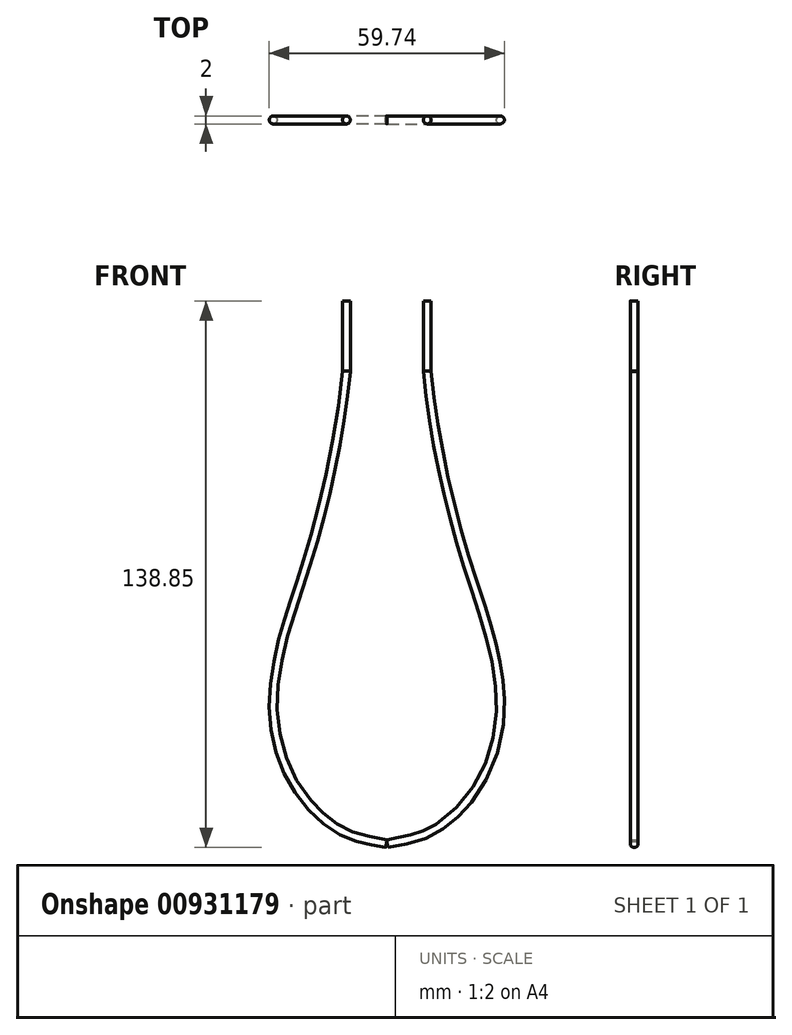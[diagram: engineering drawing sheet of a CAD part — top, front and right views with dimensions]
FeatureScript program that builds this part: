
annotation { "Feature Type Name" : "Feature", "Feature Type Description" : "" }
export const myFeature = defineFeature(function(context is Context, id is Id, definition is map)
    precondition{}
    {
        {
            var Q0;
            Q0=qCreatedBy(makeId("Front.planeOp"),FACE);
            var sketch = newSketch(context, id + "F0", { "sketchPlane" : qUnion([Q0])});
            skLineSegment(sketch, "E0", {"start": v(9.76, 64.47) * mm, "end": v(9.76, 46.63) * mm});
            skFitSpline(sketch, "E1", {"points": [v(9.76, 46.63) * mm, v(19.16, 0) * mm, v(25.18, -18.92) * mm, v(28.32, -40.13) * mm, v(22.05, -59.65) * mm, v(9.76, -70.5) * mm, v(0, -72.9) * mm], "startDerivative": vector(18.65, -207.85) * mm, "endDerivative": vector(-79.5, -16.58) * mm});
            skSolve(sketch);
        }
        {
            var Q0;
            Q0=qCreatedBy(makeId("Top.planeOp"),FACE);
            cPlane(context, id + "F1", {"entities" : qUnion([Q0]), "cplaneType" : CPlaneType.OFFSET, "offset" : 61.98 * mm, "width" : 152.4 * mm, "height" : 152.4 * mm});
        }
        {
            var Q0;
            Q0=qCreatedBy(id+"F1.planeOp",FACE);
            var sketch = newSketch(context, id + "F2", { "sketchPlane" : qUnion([Q0])});
            skCircle(sketch, "E2", {"center": v(10.27, 0) * mm, "radius": 1 * mm});
            skSolve(sketch);
        }
        {
            var Q0;
            Q0=makeQuery(id+"F2.imprint","IMPRINT",FACE,{"disambiguationData":[TD([[makeQuery(id+"F2.imprint","IMPRINT",EDGE,{"derivedFrom":sQuery(id+"F2.wireOp",EDGE,"E2")}),1.0]])]});
            var Q1;
            Q1=sQuery(id+"F0.wireOp",EDGE,"E0");
            var Q2;
            Q2=sQuery(id+"F0.wireOp",EDGE,"E1");
            sweep(context, id + "F3", {"profiles" : qUnion([Q0]), "path" : qUnion([Q1, Q2])});
        }
        {
            var Q0;
            Q0=makeQuery(id+"F3.opSweep","SWEPT_BODY",BODY,{"disambiguationData":[OSD([sQuery(id+"F0.wireOp",EDGE,"E1"),sQuery(id+"F2.wireOp",EDGE,"E2")])]});
            var Q1;
            Q1=qCreatedBy(makeId("Right.planeOp"),FACE);
            mirror(context, id + "F4", {"operationType" : NewBodyOperationType.ADD, "entities" : qUnion([Q0]), "mirrorPlane" : qUnion([Q1])});
        }
    });
